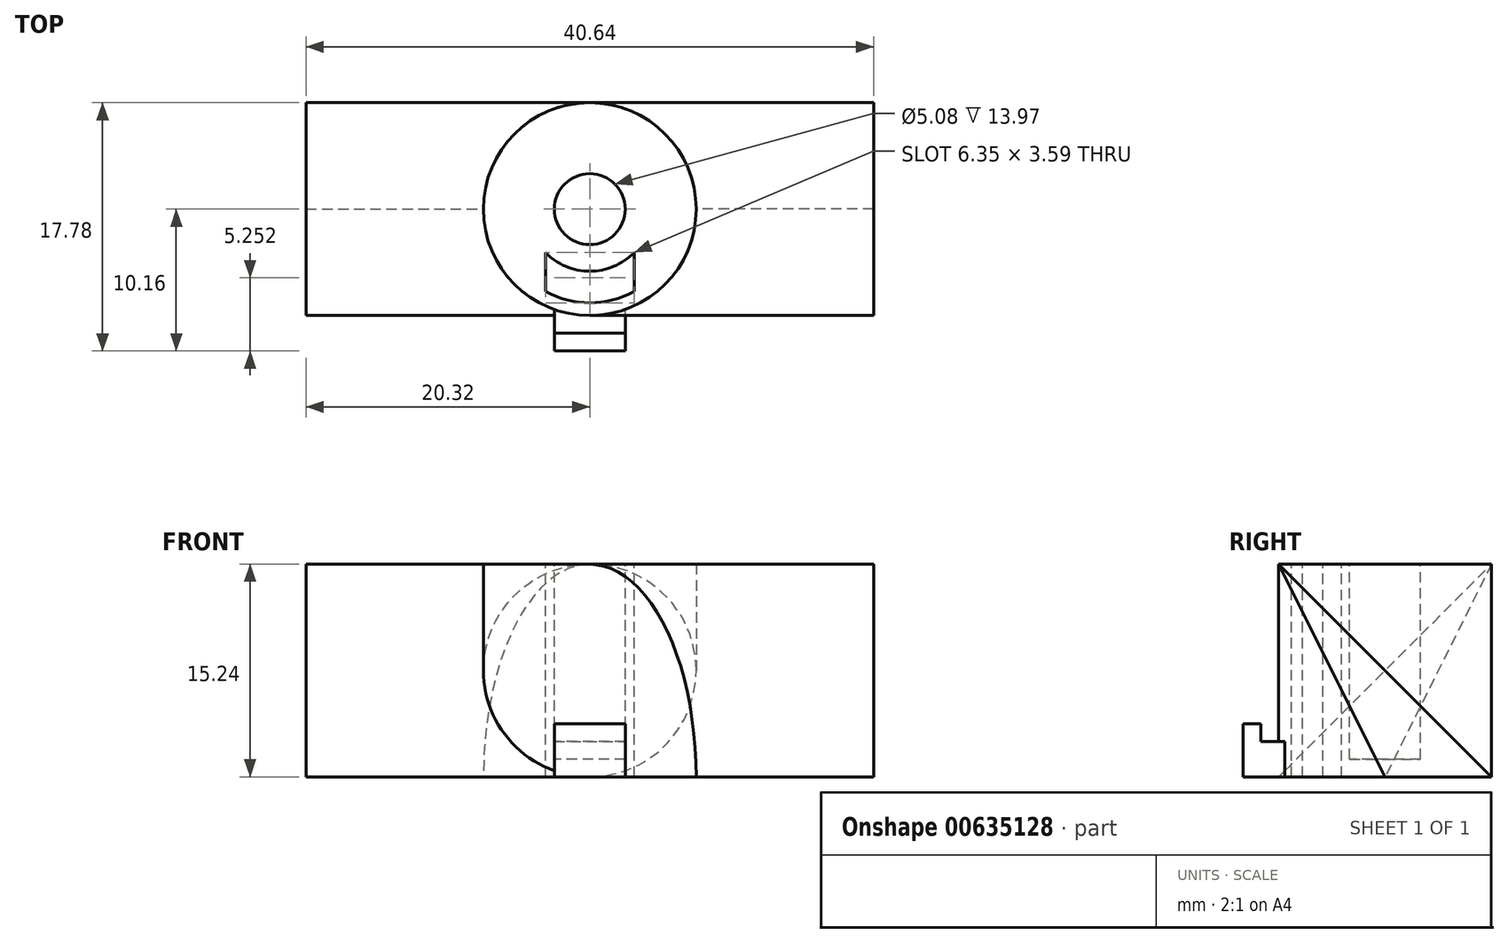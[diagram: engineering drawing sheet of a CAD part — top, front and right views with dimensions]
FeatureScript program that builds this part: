
annotation { "Feature Type Name" : "Feature", "Feature Type Description" : "" }
export const myFeature = defineFeature(function(context is Context, id is Id, definition is map)
    precondition{}
    {
        {
            var Q0;
            Q0=qCreatedBy(makeId("Top.planeOp"),FACE);
            var sketch = newSketch(context, id + "F0", { "sketchPlane" : qUnion([Q0])});
            skCircle(sketch, "E0", {"center": v(0, 0) * mm, "radius": 7.62 * mm});
            skSolve(sketch);
        }
        {
            var Q0;
            Q0=makeQuery(id+"F0.imprint","IMPRINT",FACE,{"disambiguationData":[TD([[makeQuery(id+"F0.imprint","IMPRINT",EDGE,{"derivedFrom":sQuery(id+"F0.wireOp",EDGE,"E0")}),1.0]])]});
            extrude(context, id + "F1", {"entities" : qUnion([Q0]), "depth" : 15.24 * mm, "offsetDistance" : 25.4 * mm});
        }
        {
            var Q0;
            Q0=qCreatedBy(makeId("Right.planeOp"),FACE);
            var sketch = newSketch(context, id + "F2", { "sketchPlane" : qUnion([Q0])});
            skLineSegment(sketch, "E1", {"start": v(0, 0) * mm, "end": v(7.62, 0) * mm});
            skLineSegment(sketch, "E2", {"start": v(7.62, 0) * mm, "end": v(-7.62, 15.24) * mm});
            skLineSegment(sketch, "E3", {"start": v(-7.62, 15.24) * mm, "end": v(0, 0) * mm});
            skSolve(sketch);
        }
        {
            var Q0;
            Q0 = qSketchRegion(id + "F2", true);
            extrude(context, id + "F3", {"entities" : qUnion([Q0]), "depth" : 20.32 * mm, "offsetDistance" : 25.4 * mm});
        }
        {
            var Q0;
            Q0=qCreatedBy(makeId("Front.planeOp"),FACE);
            var sketch = newSketch(context, id + "F4", { "sketchPlane" : qUnion([Q0])});
            skLineSegment(sketch, "E4", {"start": v(0, 0) * mm, "end": v(0, 35.17) * mm, "construction": true});
            skSolve(sketch);
        }
        {
            var Q0;
            Q0=makeQuery(id+"F3.opExtrude","SWEPT_BODY",BODY,{"disambiguationData":[OSD([sQuery(id+"F2.wireOp",EDGE,"E1"),sQuery(id+"F2.wireOp",EDGE,"E2"),sQuery(id+"F2.wireOp",EDGE,"E3")])]});
            var Q1;
            Q1=sQuery(id+"F4.wireOp",EDGE,"E4");
            circularPattern(context, id + "F5", {"operationType" : NewBodyOperationType.ADD, "entities" : qUnion([Q0]), "axis" : qUnion([Q1]), "angle" : 360 * degree, "instanceCount" : 2, "equalSpace" : true});
        }
        {
            var Q0;
            Q0=qCreatedBy(makeId("Front.planeOp"),FACE);
            var sketch = newSketch(context, id + "F6", { "sketchPlane" : qUnion([Q0])});
            skLineSegment(sketch, "E5.bottom", {"start": v(-2.54, 2.54) * mm, "end": v(2.54, 2.54) * mm});
            skLineSegment(sketch, "E5.top", {"start": v(-2.54, 0) * mm, "end": v(2.54, 0) * mm});
            skLineSegment(sketch, "E5.left", {"start": v(-2.54, 2.54) * mm, "end": v(-2.54, 0) * mm});
            skLineSegment(sketch, "E5.right", {"start": v(2.54, 2.54) * mm, "end": v(2.54, 0) * mm});
            skSolve(sketch);
        }
        {
            var Q0;
            Q0 = qSketchRegion(id + "F6", true);
            extrude(context, id + "F7", {"entities" : qUnion([Q0]), "operationType" : NewBodyOperationType.ADD, "depth" : 10.16 * mm, "offsetDistance" : 25.4 * mm});
        }
        {
            var Q0;
            Q0=makeQuery(id+"F7.opExtrude","SWEPT_FACE",FACE,{"disambiguationData":[OSD([sQuery(id+"F6.wireOp",EDGE,"E5.bottom")])]});
            var sketch = newSketch(context, id + "F8", { "sketchPlane" : qUnion([Q0])});
            skLineSegment(sketch, "E6.bottom", {"start": v(2.54, -10.16) * mm, "end": v(-2.54, -10.16) * mm});
            skLineSegment(sketch, "E6.top", {"start": v(2.54, -8.9) * mm, "end": v(-2.54, -8.9) * mm});
            skLineSegment(sketch, "E6.left", {"start": v(2.54, -10.16) * mm, "end": v(2.54, -8.9) * mm});
            skLineSegment(sketch, "E6.right", {"start": v(-2.54, -10.16) * mm, "end": v(-2.54, -8.9) * mm});
            skSolve(sketch);
        }
        {
            var Q0;
            Q0=makeQuery(id+"F8.imprint","IMPRINT",FACE,{"disambiguationData":[TD([[makeQuery(id+"F8.imprint","IMPRINT",EDGE,{"derivedFrom":sQuery(id+"F8.wireOp",EDGE,"E6.bottom")}),1.0]])]});
            extrude(context, id + "F9", {"entities" : qUnion([Q0]), "operationType" : NewBodyOperationType.ADD, "depth" : 1.27 * mm, "offsetDistance" : 25.4 * mm});
        }
        {
            var Q0;
            Q0=makeQuery(id+"F1.opExtrude","CAP_FACE",FACE,{"disambiguationData":[OSD([sQuery(id+"F0.wireOp",EDGE,"E0")])],"isStart":false});
            var sketch = newSketch(context, id + "F10", { "sketchPlane" : qUnion([Q0])});
            skCircle(sketch, "E7", {"center": v(0, 0) * mm, "radius": 2.54 * mm});
            skSolve(sketch);
        }
        {
            var Q0;
            Q0 = qSketchRegion(id + "F10", true);
            extrude(context, id + "F11", {"entities" : qUnion([Q0]), "operationType" : NewBodyOperationType.REMOVE, "oppositeDirection" : true, "depth" : 13.97 * mm, "offsetDistance" : 25.4 * mm});
        }
        {
            var Q0;
            Q0=makeQuery(id+"F1.opExtrude","CAP_FACE",FACE,{"disambiguationData":[OSD([sQuery(id+"F0.wireOp",EDGE,"E0")])],"isStart":false});
            var sketch = newSketch(context, id + "F12", { "sketchPlane" : qUnion([Q0])});
            skLineSegment(sketch, "E8", {"start": v(-3.18, -3.11) * mm, "end": v(-3.18, -5.9) * mm});
            skLineSegment(sketch, "E9", {"start": v(3.18, -3.11) * mm, "end": v(3.18, -5.9) * mm});
            skArc(sketch, "E10", {"start": v(-3.18, -3.11) * mm, "mid": v(0, -4.44) * mm, "end": v(3.18, -3.11) * mm});
            skArc(sketch, "E11", {"start": v(-3.18, -5.9) * mm, "mid": v(0, -6.7) * mm, "end": v(3.18, -5.9) * mm});
            skSolve(sketch);
        }
        {
            var Q0;
            Q0=makeQuery(id+"F12.imprint","IMPRINT",FACE,{"disambiguationData":[TD([[makeQuery(id+"F12.imprint","IMPRINT",EDGE,{"derivedFrom":sQuery(id+"F12.wireOp",EDGE,"E8")}),1.0]])]});
            extrude(context, id + "F13", {"entities" : qUnion([Q0]), "operationType" : NewBodyOperationType.REMOVE, "oppositeDirection" : true, "depth" : 25.4 * mm, "offsetDistance" : 25.4 * mm});
        }
    });
